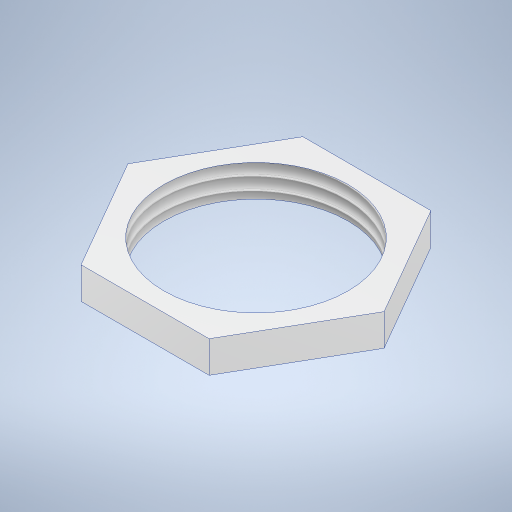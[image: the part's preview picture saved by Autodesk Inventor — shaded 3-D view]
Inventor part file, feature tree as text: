
AUTODESK INVENTOR PART (.ipt)
format: ipt  version: 2024 (Build 280153000, 153)  size: 251,904 bytes
history: native  units: in
note: dims shown in document units (in); Inventor stores cm internally (conversion verified against a paired STEP export)
features: extrude x1, thread x1, sketch x1
ambient origin geometry x8: Origin, YZ Plane, XZ Plane, XY Plane, X Axis, Y Axis, Z Axis, Center Point
bodies: Solid1 (feature_tree)
feature tree (3):
  extrude  "Extrusion1"  Depth=0.125in
  thread  "Thread1"  [1 undecoded]
  sketch  "Sketch1"  dims[d0=0.4375in d1=0.727in d2=0.125in d3=0.0in d4=0.125in d5=0.0in]
note: 1 required parameter value undecoded (feature->parameter linkage not recoverable at this tier; creation-order binding heuristic only, values carry confidence <= 0.55)
